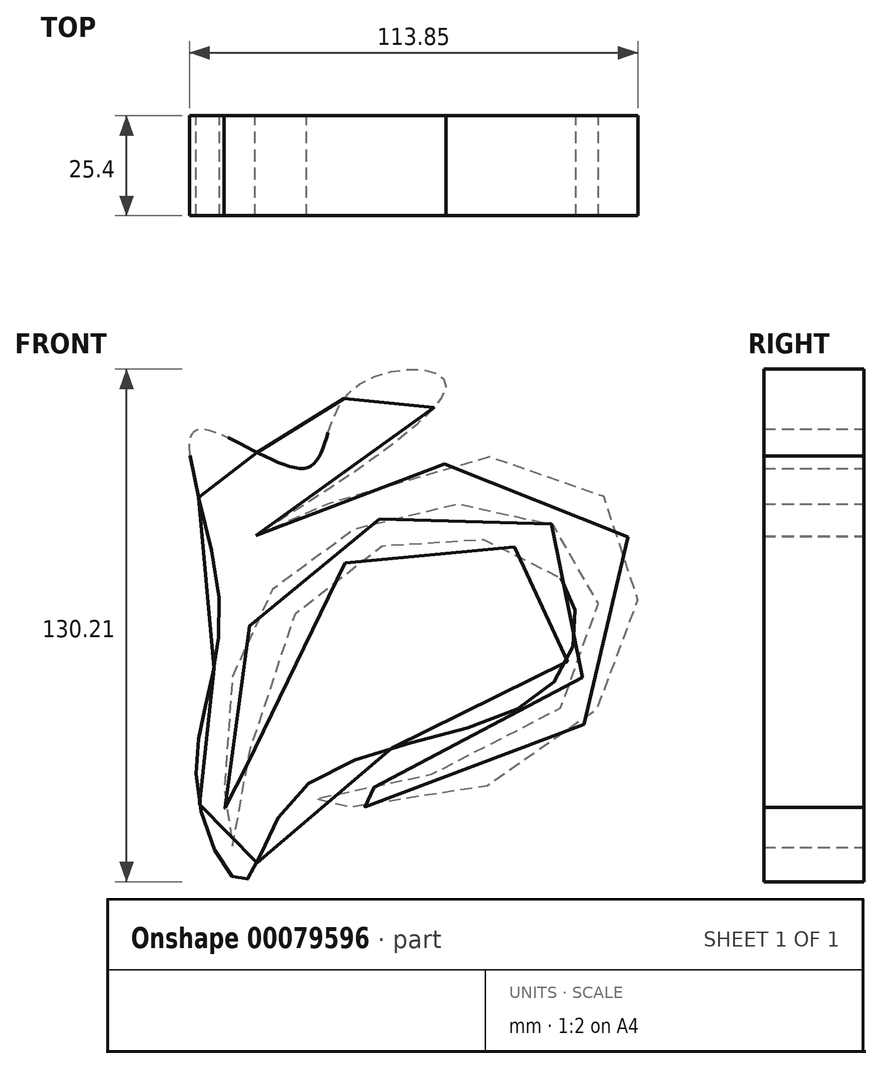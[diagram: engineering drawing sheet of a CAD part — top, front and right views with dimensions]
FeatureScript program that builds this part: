
annotation { "Feature Type Name" : "Feature", "Feature Type Description" : "" }
export const myFeature = defineFeature(function(context is Context, id is Id, definition is map)
    precondition{}
    {
        {
            var Q0;
            Q0=qCreatedBy(makeId("Front.planeOp"),FACE);
            var sketch = newSketch(context, id + "F0", { "sketchPlane" : qUnion([Q0])});
            skFitSpline(sketch, "E0", {"points": [v(-59.41, 23.12) * mm, v(4.48, 43.3) * mm, v(37.55, 9.67) * mm, v(2.52, -39.37) * mm, v(-46.52, -44.7) * mm, v(11.77, -26.2) * mm, v(24.1, 17.52) * mm, v(-9.8, 30.97) * mm, v(-52.4, 12.47) * mm, v(-67.26, -26.48) * mm, v(-65.58, -56.19) * mm, v(-51.28, 0) * mm, v(-10.37, 22.84) * mm, v(19.62, 9.95) * mm, v(12.33, -17.8) * mm, v(-48.76, -42.18) * mm, v(-62.77, -64.88) * mm, v(-73.7, -45.82) * mm, v(-71.74, -18.08) * mm, v(-69.78, 14.71) * mm, v(-74.26, 50.02) * mm, v(-46.8, 40.22) * mm, v(-34.75, 60.4) * mm, v(-11.2, 60.95) * mm, v(-59.41, 23.12) * mm]});
            skSolve(sketch);
        }
        {
            var Q0;
            Q0=makeQuery(id+"F0.imprint","IMPRINT",FACE,{"disambiguationData":[TD([[makeQuery(id+"F0.imprint","IMPRINT",EDGE,{"derivedFrom":sQuery(id+"F0.wireOp",EDGE,"E0")}),-1.0]])]});
            extrude(context, id + "F1", {"entities" : qUnion([Q0]), "depth" : 25.4 * mm});
        }
        {
            var Q0;
            Q0=qCreatedBy(makeId("Front.planeOp"),FACE);
            var sketch = newSketch(context, id + "F2", { "sketchPlane" : qUnion([Q0])});
            skLineSegment(sketch, "E1", {"start": v(-59.6, 22.94) * mm, "end": v(0, 57.03) * mm});
            skLineSegment(sketch, "E2", {"start": v(0, 57.03) * mm, "end": v(-7.32, 48.34) * mm});
            skLineSegment(sketch, "E3", {"start": v(-7.32, 48.34) * mm, "end": v(-59.6, 22.94) * mm});
            skSolve(sketch);
        }
        {
            var Q0;
            Q0=makeQuery(id+"F2.imprint","IMPRINT",FACE,{"disambiguationData":[TD([[makeQuery(id+"F2.imprint","IMPRINT",EDGE,{"derivedFrom":sQuery(id+"F2.wireOp",EDGE,"E1")}),-1.0]])]});
            extrude(context, id + "F3", {"entities" : qUnion([Q0]), "depth" : 25.4 * mm});
        }
        {
            var Q0;
            Q0=makeQuery(id+"F3.opExtrude","SWEPT_BODY",BODY,{"disambiguationData":[OSD([sQuery(id+"F2.wireOp",EDGE,"E1"),sQuery(id+"F2.wireOp",EDGE,"E2"),sQuery(id+"F2.wireOp",EDGE,"E3")])]});
            deleteBodies(context, id + "F4", {"entities" : qUnion([Q0])});
        }
    });
